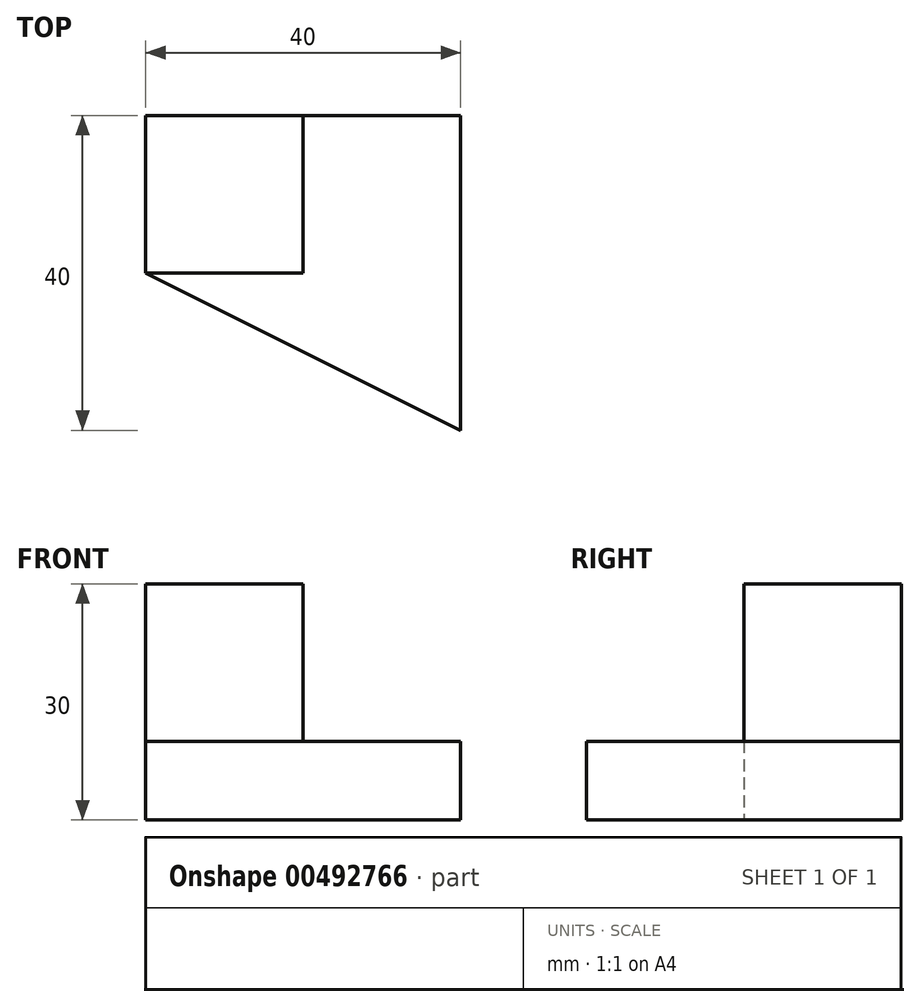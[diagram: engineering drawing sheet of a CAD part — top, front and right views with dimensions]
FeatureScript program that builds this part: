
annotation { "Feature Type Name" : "Feature", "Feature Type Description" : "" }
export const myFeature = defineFeature(function(context is Context, id is Id, definition is map)
    precondition{}
    {
        {
            var Q0;
            Q0=qCreatedBy(makeId("Top.planeOp"),FACE);
            var sketch = newSketch(context, id + "F0", { "sketchPlane" : qUnion([Q0])});
            skLineSegment(sketch, "E0", {"start": v(0, 0) * mm, "end": v(0, 20) * mm});
            skLineSegment(sketch, "E1", {"start": v(0, 20) * mm, "end": v(40, 20) * mm});
            skLineSegment(sketch, "E2", {"start": v(40, 20) * mm, "end": v(40, -20) * mm});
            skLineSegment(sketch, "E3", {"start": v(0, 0) * mm, "end": v(40, -20) * mm});
            skSolve(sketch);
        }
        {
            var Q0;
            Q0 = qSketchRegion(id + "F0", true);
            extrude(context, id + "F1", {"entities" : qUnion([Q0]), "depth" : 10 * mm});
        }
        {
            var Q0;
            Q0=makeQuery(id+"F1.opExtrude","CAP_FACE",FACE,{"disambiguationData":[OSD([sQuery(id+"F0.wireOp",EDGE,"E0"),sQuery(id+"F0.wireOp",EDGE,"E1"),sQuery(id+"F0.wireOp",EDGE,"E2"),sQuery(id+"F0.wireOp",EDGE,"E3")])],"isStart":false});
            var sketch = newSketch(context, id + "F2", { "sketchPlane" : qUnion([Q0])});
            skSolve(sketch);
        }
        {
            var Q0;
            Q0=makeQuery(id+"F2.imprint","IMPRINT",FACE,{"disambiguationData":[TD([[makeQuery(id+"F2.imprint","IMPRINT",EDGE,{"derivedFrom":makeQuery(id+"F1.opExtrude","CAP_EDGE",EDGE,{"disambiguationData":[OSD([sQuery(id+"F0.wireOp",EDGE,"E0")])],"isStart":false})}),-1.0]])]});
            var sketch = newSketch(context, id + "F3", { "sketchPlane" : qUnion([Q0])});
            skLineSegment(sketch, "E4", {"start": v(0, 20) * mm, "end": v(20, 20) * mm});
            skLineSegment(sketch, "E5", {"start": v(20, 20) * mm, "end": v(20, 0) * mm});
            skLineSegment(sketch, "E6", {"start": v(20, 0) * mm, "end": v(0, 0) * mm});
            skSolve(sketch);
        }
        {
            var Q0;
            Q0 = qSketchRegion(id + "F3", true);
            var Q1;
            Q1=makeQuery(id+"F3.imprint","IMPRINT",FACE,{"disambiguationData":[TD([[makeQuery(id+"F3.imprint","IMPRINT",EDGE,{"derivedFrom":sQuery(id+"F3.wireOp",EDGE,"E4")}),-1.0]])]});
            extrude(context, id + "F4", {"entities" : qUnion([Q0, Q1]), "operationType" : NewBodyOperationType.ADD, "depth" : 20 * mm});
        }
    });
